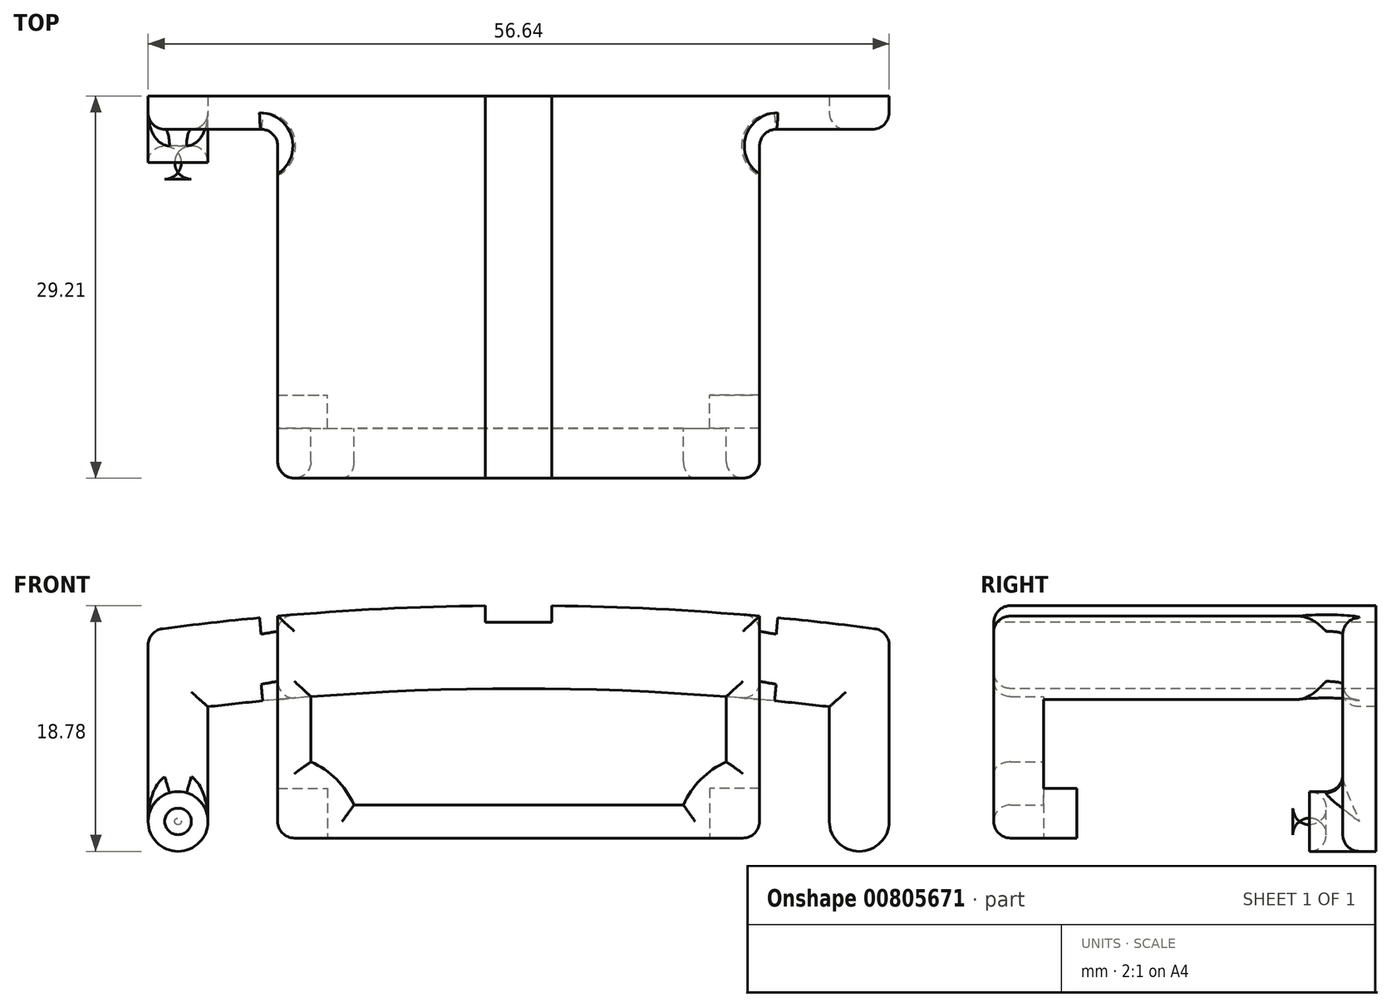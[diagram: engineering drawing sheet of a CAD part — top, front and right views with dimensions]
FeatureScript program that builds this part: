
annotation { "Feature Type Name" : "Feature", "Feature Type Description" : "" }
export const myFeature = defineFeature(function(context is Context, id is Id, definition is map)
    precondition{}
    {
        {
            var Q0;
            Q0=qCreatedBy(makeId("Front.planeOp"),FACE);
            var sketch = newSketch(context, id + "F0", { "sketchPlane" : qUnion([Q0])});
            skArc(sketch, "E0", {"start": v(18.42, 0) * mm, "mid": v(0, 0.84) * mm, "end": v(-18.42, 0) * mm});
            skLineSegment(sketch, "E1", {"start": v(-18.42, 0) * mm, "end": v(-18.41, -26.23) * mm});
            skLineSegment(sketch, "E2.MirrorCS", {"start": v(18.41, 0) * mm, "end": v(18.41, -26.23) * mm});
            skLineSegment(sketch, "E3", {"start": v(-18.41, -26.23) * mm, "end": v(18.41, -26.23) * mm});
            skSolve(sketch);
        }
        {
            var Q0;
            Q0=qCreatedBy(makeId("Front.planeOp"),FACE);
            var sketch = newSketch(context, id + "F1", { "sketchPlane" : qUnion([Q0])});
            skArc(sketch, "E4", {"start": v(18.42, 6.38) * mm, "mid": v(0, 7.19) * mm, "end": v(-18.42, 6.38) * mm});
            skLineSegment(sketch, "E5", {"start": v(-18.42, 6.38) * mm, "end": v(-18.42, -10.6) * mm});
            skLineSegment(sketch, "E6.MirrorCS", {"start": v(18.41, 6.38) * mm, "end": v(18.41, -10.6) * mm});
            skLineSegment(sketch, "E7", {"start": v(-18.41, -10.6) * mm, "end": v(18.41, -10.6) * mm});
            skSolve(sketch);
        }
        {
            var Q0;
            Q0=makeQuery(id+"F1.imprint","IMPRINT",FACE,{"disambiguationData":[TD([[makeQuery(id+"F1.imprint","IMPRINT",EDGE,{"derivedFrom":sQuery(id+"F1.wireOp",EDGE,"E4")}),1.0]])]});
            extrude(context, id + "F2", {"entities" : qUnion([Q0]), "depth" : 6.35 * mm, "offsetDistance" : 25.4 * mm, "hasSecondDirection" : true, "secondDirectionOppositeDirection" : true, "secondDirectionDepth" : 20.32 * mm});
        }
        {
            var Q0;
            Q0=makeQuery(id+"F0.imprint","IMPRINT",FACE,{"disambiguationData":[TD([[makeQuery(id+"F0.imprint","IMPRINT",EDGE,{"derivedFrom":sQuery(id+"F0.wireOp",EDGE,"E0")}),1.0]])]});
            extrude(context, id + "F3", {"entities" : qUnion([Q0]), "operationType" : NewBodyOperationType.REMOVE, "oppositeDirection" : true, "depth" : 25.4 * mm, "offsetDistance" : 25.4 * mm});
        }
        {
            var Q0;
            Q0=makeQuery(id+"F2.opExtrude","CAP_FACE",FACE,{"disambiguationData":[OSD([sQuery(id+"F1.wireOp",EDGE,"E4"),sQuery(id+"F1.wireOp",EDGE,"E5"),sQuery(id+"F1.wireOp",EDGE,"E6.MirrorCS"),sQuery(id+"F1.wireOp",EDGE,"E7")])],"isStart":true});
            var sketch = newSketch(context, id + "F4", { "sketchPlane" : qUnion([Q0])});
            skCircle(sketch, "E8", {"center": v(26.04, -9.32) * mm, "radius": 2.29 * mm});
            skCircle(sketch, "E9.MirrorC", {"center": v(-26.04, -9.32) * mm, "radius": 2.29 * mm});
            skLineSegment(sketch, "E10", {"start": v(-19.6, 0.84) * mm, "end": v(20.78, 0.84) * mm, "construction": true});
            skSolve(sketch);
        }
        {
            var Q0;
            Q0=makeQuery(id+"F4.imprint","IMPRINT",FACE,{"disambiguationData":[TD([[makeQuery(id+"F4.imprint","IMPRINT",EDGE,{"derivedFrom":sQuery(id+"F4.wireOp",EDGE,"E8")}),1.0]])]});
            var Q1;
            Q1=makeQuery(id+"F4.imprint","IMPRINT",FACE,{"disambiguationData":[TD([[makeQuery(id+"F4.imprint","IMPRINT",EDGE,{"derivedFrom":sQuery(id+"F4.wireOp",EDGE,"E9.MirrorC")}),-1.0]])]});
            extrude(context, id + "F5", {"entities" : qUnion([Q0, Q1]), "oppositeDirection" : true, "depth" : 3.8 * mm, "offsetDistance" : 25.4 * mm});
        }
        {
            var Q0;
            Q0=makeQuery(id+"F2.opExtrude","CAP_FACE",FACE,{"disambiguationData":[OSD([sQuery(id+"F1.wireOp",EDGE,"E4"),sQuery(id+"F1.wireOp",EDGE,"E5"),sQuery(id+"F1.wireOp",EDGE,"E6.MirrorCS"),sQuery(id+"F1.wireOp",EDGE,"E7")])],"isStart":true});
            var sketch = newSketch(context, id + "F6", { "sketchPlane" : qUnion([Q0])});
            skArc(sketch, "E11", {"start": v(28.32, 5.26) * mm, "mid": v(0, 7.19) * mm, "end": v(-28.32, 5.26) * mm});
            skArc(sketch, "E12.0", {"start": v(-28.32, -9.32) * mm, "mid": v(-26.04, -11.6) * mm, "end": v(-23.75, -9.32) * mm});
            skLineSegment(sketch, "E13", {"start": v(-28.32, -9.32) * mm, "end": v(-28.32, 5.26) * mm});
            skLineSegment(sketch, "E14", {"start": v(-23.75, -9.32) * mm, "end": v(-23.75, -0.56) * mm});
            skPoint(sketch, "E15.orphan", {"position": v(-65.08, -3.17) * mm});
            skLineSegment(sketch, "E16.MirrorCS", {"start": v(23.75, -9.32) * mm, "end": v(23.75, -0.56) * mm});
            skLineSegment(sketch, "E17.MirrorCS", {"start": v(28.32, -9.32) * mm, "end": v(28.32, 5.26) * mm});
            skArc(sketch, "E18.MirrorCS", {"start": v(28.32, -9.32) * mm, "mid": v(26.04, -11.6) * mm, "end": v(23.75, -9.32) * mm});
            skArc(sketch, "E19.trimOffspring", {"start": v(23.75, -0.56) * mm, "mid": v(0, 0.84) * mm, "end": v(-23.75, -0.56) * mm});
            skSolve(sketch);
        }
        {
            var Q0;
            Q0=makeQuery(id+"F6.imprint","IMPRINT",FACE,{"disambiguationData":[TD([[makeQuery(id+"F6.imprint","IMPRINT",EDGE,{"derivedFrom":sQuery(id+"F6.wireOp",EDGE,"E12.0")}),1.0]])]});
            var Q1;
            {var subQ2=makeQuery(id+"F2.opExtrude","CAP_EDGE",EDGE,{"disambiguationData":[OSD([sQuery(id+"F1.wireOp",EDGE,"E5")])],"isStart":true});Q1=makeQuery(id+"F6.imprint","IMPRINT",FACE,{"disambiguationData":[TD([[makeQuery(id+"F6.imprint","IMPRINT",EDGE,{"derivedFrom":subQ2}),-1.0]])]});}
            var Q2;
            {var subQ1=sQuery(id+"F6.wireOp",EDGE,"E16.MirrorCS");Q2=makeQuery(id+"F6.imprint","IMPRINT",FACE,{"disambiguationData":[TD([[makeQuery(id+"F6.imprint","IMPRINT",EDGE,{"derivedFrom":subQ1}),-1.0]])]});}
            extrude(context, id + "F7", {"entities" : qUnion([Q0, Q1, Q2]), "operationType" : NewBodyOperationType.ADD, "depth" : 2.54 * mm, "offsetDistance" : 25.4 * mm});
        }
        {
            var Q0;
            Q0=makeQuery(id+"F3.boolean.opBoolean","COPY",FACE,{"derivedFrom":makeQuery(id+"F3.opExtrude","CAP_FACE",FACE,{"disambiguationData":[OSD([sQuery(id+"F0.wireOp",EDGE,"E0"),sQuery(id+"F0.wireOp",EDGE,"E1"),sQuery(id+"F0.wireOp",EDGE,"E2.MirrorCS"),sQuery(id+"F0.wireOp",EDGE,"E3")])],"isStart":true})});
            var sketch = newSketch(context, id + "F8", { "sketchPlane" : qUnion([Q0])});
            skLineSegment(sketch, "E20.0.0", {"start": v(18.41, -6.78) * mm, "end": v(18.42, 0) * mm});
            skArc(sketch, "E20.0.1", {"start": v(18.42, 0) * mm, "mid": v(0, 0.84) * mm, "end": v(-18.42, 0) * mm});
            skLineSegment(sketch, "E20.0.2", {"start": v(-18.41, 0) * mm, "end": v(-18.41, -6.78) * mm});
            skLineSegment(sketch, "E20.0.3", {"start": v(-14.6, -10.6) * mm, "end": v(14.6, -10.6) * mm});
            skLineSegment(sketch, "E21", {"start": v(-18.41, -6.78) * mm, "end": v(-14.6, -6.78) * mm});
            skLineSegment(sketch, "E22", {"start": v(-14.6, -6.78) * mm, "end": v(-14.6, -10.6) * mm});
            skLineSegment(sketch, "E23.MirrorCS", {"start": v(18.41, -6.78) * mm, "end": v(14.6, -6.78) * mm});
            skLineSegment(sketch, "E24.MirrorCS", {"start": v(14.6, -6.78) * mm, "end": v(14.6, -10.6) * mm});
            skPoint(sketch, "E25.orphan", {"position": v(-18.41, -10.6) * mm});
            skPoint(sketch, "E26.orphan", {"position": v(18.41, -10.6) * mm});
            skArc(sketch, "E27", {"start": v(-14.6, -10.6) * mm, "mid": v(-15.72, -7.9) * mm, "end": v(-18.41, -6.78) * mm, "construction": true});
            skArc(sketch, "E28.MirrorCS", {"start": v(14.6, -10.6) * mm, "mid": v(15.72, -7.9) * mm, "end": v(18.41, -6.78) * mm, "construction": true});
            skSolve(sketch);
        }
        {
            var Q0;
            Q0=makeQuery(id+"F8.imprint","IMPRINT",FACE,{"disambiguationData":[TD([[makeQuery(id+"F8.imprint","IMPRINT",EDGE,{"derivedFrom":sQuery(id+"F8.wireOp",EDGE,"E20.0.0")}),-1.0]])]});
            extrude(context, id + "F9", {"entities" : qUnion([Q0]), "operationType" : NewBodyOperationType.REMOVE, "oppositeDirection" : true, "depth" : 2.54 * mm, "offsetDistance" : 25.4 * mm});
        }
        {
            var Q0;
            Q0=makeQuery(id+"F9.boolean.opBoolean","COPY",FACE,{"derivedFrom":makeQuery(id+"F9.opExtrude","CAP_FACE",FACE,{"disambiguationData":[OSD([sQuery(id+"F8.wireOp",EDGE,"E20.0.0"),sQuery(id+"F8.wireOp",EDGE,"E20.0.1"),sQuery(id+"F8.wireOp",EDGE,"E20.0.2"),sQuery(id+"F8.wireOp",EDGE,"E20.0.3"),sQuery(id+"F8.wireOp",EDGE,"E21"),sQuery(id+"F8.wireOp",EDGE,"E22"),sQuery(id+"F8.wireOp",EDGE,"E23.MirrorCS"),sQuery(id+"F8.wireOp",EDGE,"E24.MirrorCS")])],"isStart":false})});
            var sketch = newSketch(context, id + "F10", { "sketchPlane" : qUnion([Q0])});
            skLineSegment(sketch, "E29", {"start": v(-15.88, 0.22) * mm, "end": v(-15.88, -4.77) * mm});
            skArc(sketch, "E30", {"start": v(-12.6, -8.05) * mm, "mid": v(-13.92, -6.1) * mm, "end": v(-15.88, -4.77) * mm});
            skArc(sketch, "E31.MirrorCS", {"start": v(12.6, -8.05) * mm, "mid": v(13.92, -6.1) * mm, "end": v(15.88, -4.77) * mm});
            skLineSegment(sketch, "E32.MirrorCS", {"start": v(15.88, 0.22) * mm, "end": v(15.88, -4.77) * mm});
            skLineSegment(sketch, "E33", {"start": v(-12.6, -8.05) * mm, "end": v(12.6, -8.05) * mm});
            skArc(sketch, "E34.0", {"start": v(15.87, 0.22) * mm, "mid": v(0, 0.84) * mm, "end": v(-15.87, 0.22) * mm});
            skPoint(sketch, "E35.orphan", {"position": v(-23.75, -0.56) * mm});
            skPoint(sketch, "E36.orphan", {"position": v(-15.88, 1.16) * mm});
            skPoint(sketch, "E37.orphan", {"position": v(15.88, 1.16) * mm});
            skPoint(sketch, "E38.orphan", {"position": v(23.75, -0.56) * mm});
            skSolve(sketch);
        }
        {
            var Q0;
            Q0=makeQuery(id+"F10.imprint","IMPRINT",FACE,{"disambiguationData":[TD([[makeQuery(id+"F10.imprint","IMPRINT",EDGE,{"derivedFrom":sQuery(id+"F10.wireOp",EDGE,"E29")}),1.0]])]});
            extrude(context, id + "F11", {"entities" : qUnion([Q0]), "operationType" : NewBodyOperationType.REMOVE, "endBound" : BoundingType.UP_TO_NEXT, "oppositeDirection" : true, "depth" : 25.4 * mm, "offsetDistance" : 25.4 * mm});
        }
        {
            var Q0;
            Q0=makeQuery(id+"F2.opExtrude","CAP_FACE",FACE,{"disambiguationData":[OSD([sQuery(id+"F1.wireOp",EDGE,"E4"),sQuery(id+"F1.wireOp",EDGE,"E5"),sQuery(id+"F1.wireOp",EDGE,"E6.MirrorCS"),sQuery(id+"F1.wireOp",EDGE,"E7")])],"isStart":false});
            var Q1;
            {var subQ0=sQuery(id+"F6.wireOp",EDGE,"E19.trimOffspring");var subQ1=sQuery(id+"F6.wireOp",EDGE,"E14");var subQ2=sQuery(id+"F6.wireOp",EDGE,"E11");var subQ3=sQuery(id+"F6.wireOp",EDGE,"E12.0");var subQ4=sQuery(id+"F6.wireOp",EDGE,"E13");Q1=makeQuery(id+"F7.boolean.opBoolean","SPLIT",FACE,{"disambiguationData":[TD([makeQuery(id+"F2.opExtrude","SWEPT_FACE",FACE,{"disambiguationData":[OSD([sQuery(id+"F1.wireOp",EDGE,"E6.MirrorCS")])]})])],"derivedFrom":makeQuery(id+"F7.opExtrude","CAP_FACE",FACE,{"disambiguationData":[OSD([subQ2,subQ3,subQ4,subQ1,sQuery(id+"F6.wireOp",EDGE,"E16.MirrorCS"),sQuery(id+"F6.wireOp",EDGE,"E17.MirrorCS"),sQuery(id+"F6.wireOp",EDGE,"E18.MirrorCS"),subQ0])],"isStart":true})});}
            var Q2;
            Q2=makeQuery(id+"F9.boolean.opBoolean","COPY",EDGE,{"derivedFrom":makeQuery(id+"F9.opExtrude","CAP_EDGE",EDGE,{"disambiguationData":[OSD([sQuery(id+"F8.wireOp",EDGE,"E28.MirrorCS")])],"isStart":true})});
            var Q3;
            Q3=makeQuery(id+"F9.boolean.opBoolean","COPY",EDGE,{"derivedFrom":makeQuery(id+"F9.opExtrude","CAP_EDGE",EDGE,{"disambiguationData":[OSD([sQuery(id+"F8.wireOp",EDGE,"E27")])],"isStart":true})});
            var Q4;
            {var subQ0=sQuery(id+"F6.wireOp",EDGE,"E19.trimOffspring");var subQ1=sQuery(id+"F6.wireOp",EDGE,"E11");var subQ2=sQuery(id+"F6.wireOp",EDGE,"E16.MirrorCS");var subQ3=sQuery(id+"F6.wireOp",EDGE,"E17.MirrorCS");var subQ4=sQuery(id+"F6.wireOp",EDGE,"E18.MirrorCS");Q4=makeQuery(id+"F7.boolean.opBoolean","SPLIT",FACE,{"disambiguationData":[TD([makeQuery(id+"F2.opExtrude","SWEPT_FACE",FACE,{"disambiguationData":[OSD([sQuery(id+"F1.wireOp",EDGE,"E5")])]})])],"derivedFrom":makeQuery(id+"F7.opExtrude","CAP_FACE",FACE,{"disambiguationData":[OSD([subQ1,sQuery(id+"F6.wireOp",EDGE,"E12.0"),sQuery(id+"F6.wireOp",EDGE,"E13"),sQuery(id+"F6.wireOp",EDGE,"E14"),subQ2,subQ3,subQ4,subQ0])],"isStart":true})});}
            var Q5;
            Q5=makeQuery(id+"F5.opExtrude","CAP_FACE",FACE,{"disambiguationData":[OSD([sQuery(id+"F4.wireOp",EDGE,"E9.MirrorC")])],"isStart":false});
            var Q6;
            Q6=makeQuery(id+"F5.opExtrude","CAP_EDGE",EDGE,{"disambiguationData":[OSD([sQuery(id+"F4.wireOp",EDGE,"E8")])],"isStart":false});
            var Q7;
            Q7=makeQuery(id+"F7.opExtrude","SWEPT_EDGE",EDGE,{"disambiguationData":[OSD([sQuery(id+"F6.wireOp",EDGE,"E11"),sQuery(id+"F6.wireOp",EDGE,"E17.MirrorCS")])]});
            var Q8;
            Q8=makeQuery(id+"F7.opExtrude","SWEPT_EDGE",EDGE,{"disambiguationData":[OSD([sQuery(id+"F6.wireOp",EDGE,"E11"),sQuery(id+"F6.wireOp",EDGE,"E13")])]});
            var Q9;
            Q9=makeQuery(id+"F9.boolean.opBoolean","COPY",EDGE,{"derivedFrom":makeQuery(id+"F9.opExtrude","CAP_EDGE",EDGE,{"disambiguationData":[OSD([sQuery(id+"F8.wireOp",EDGE,"E20.0.0")])],"isStart":false})});
            var Q10;
            Q10=makeQuery(id+"F9.boolean.opBoolean","COPY",EDGE,{"derivedFrom":makeQuery(id+"F9.opExtrude","CAP_EDGE",EDGE,{"disambiguationData":[OSD([sQuery(id+"F8.wireOp",EDGE,"E20.0.3")])],"isStart":false})});
            var Q11;
            Q11=makeQuery(id+"F9.boolean.opBoolean","COPY",EDGE,{"derivedFrom":makeQuery(id+"F9.opExtrude","CAP_EDGE",EDGE,{"disambiguationData":[OSD([sQuery(id+"F8.wireOp",EDGE,"E20.0.2")])],"isStart":false})});
            var Q12;
            Q12=makeQuery(id+"F2.opExtrude","SWEPT_EDGE",EDGE,{"disambiguationData":[OSD([sQuery(id+"F1.wireOp",EDGE,"E6.MirrorCS"),sQuery(id+"F1.wireOp",EDGE,"E7")])]});
            var Q13;
            Q13=makeQuery(id+"F2.opExtrude","SWEPT_EDGE",EDGE,{"disambiguationData":[OSD([sQuery(id+"F1.wireOp",EDGE,"E5"),sQuery(id+"F1.wireOp",EDGE,"E7")])]});
            fillet(context, id + "F12", {"entities" : qUnion([Q0, Q1, Q2, Q3, Q4, Q5, Q6, Q7, Q8, Q9, Q10, Q11, Q12, Q13]), "radius" : 1.27 * mm, "tangentPropagation" : true, "allowEdgeOverflow" : false});
        }
        {
            var Q0;
            Q0=makeQuery(id+"F12.opFillet","SPLIT",FACE,{"disambiguationData":[OD(0.0)],"derivedFrom":makeQuery(id+"F2.opExtrude","CAP_FACE",FACE,{"disambiguationData":[OSD([sQuery(id+"F1.wireOp",EDGE,"E4"),sQuery(id+"F1.wireOp",EDGE,"E5"),sQuery(id+"F1.wireOp",EDGE,"E6.MirrorCS"),sQuery(id+"F1.wireOp",EDGE,"E7")])],"isStart":false})});
            var sketch = newSketch(context, id + "F13", { "sketchPlane" : qUnion([Q0])});
            skLineSegment(sketch, "E39.bottom", {"start": v(-2.54, 11) * mm, "end": v(2.54, 11) * mm});
            skLineSegment(sketch, "E39.top", {"start": v(-2.54, 5.92) * mm, "end": v(2.54, 5.92) * mm});
            skLineSegment(sketch, "E39.left", {"start": v(-2.54, 11) * mm, "end": v(-2.54, 5.92) * mm});
            skLineSegment(sketch, "E39.right", {"start": v(2.54, 11) * mm, "end": v(2.54, 5.92) * mm});
            skSolve(sketch);
        }
        {
            var Q0;
            Q0=makeQuery(id+"F13.imprint","IMPRINT",FACE,{"disambiguationData":[TD([[makeQuery(id+"F13.imprint","IMPRINT",EDGE,{"derivedFrom":sQuery(id+"F13.wireOp",EDGE,"E39.bottom")}),-1.0]])]});
            extrude(context, id + "F14", {"entities" : qUnion([Q0]), "operationType" : NewBodyOperationType.REMOVE, "endBound" : BoundingType.THROUGH_ALL, "oppositeDirection" : true, "depth" : 25.4 * mm, "offsetDistance" : 25.4 * mm});
        }
    });
